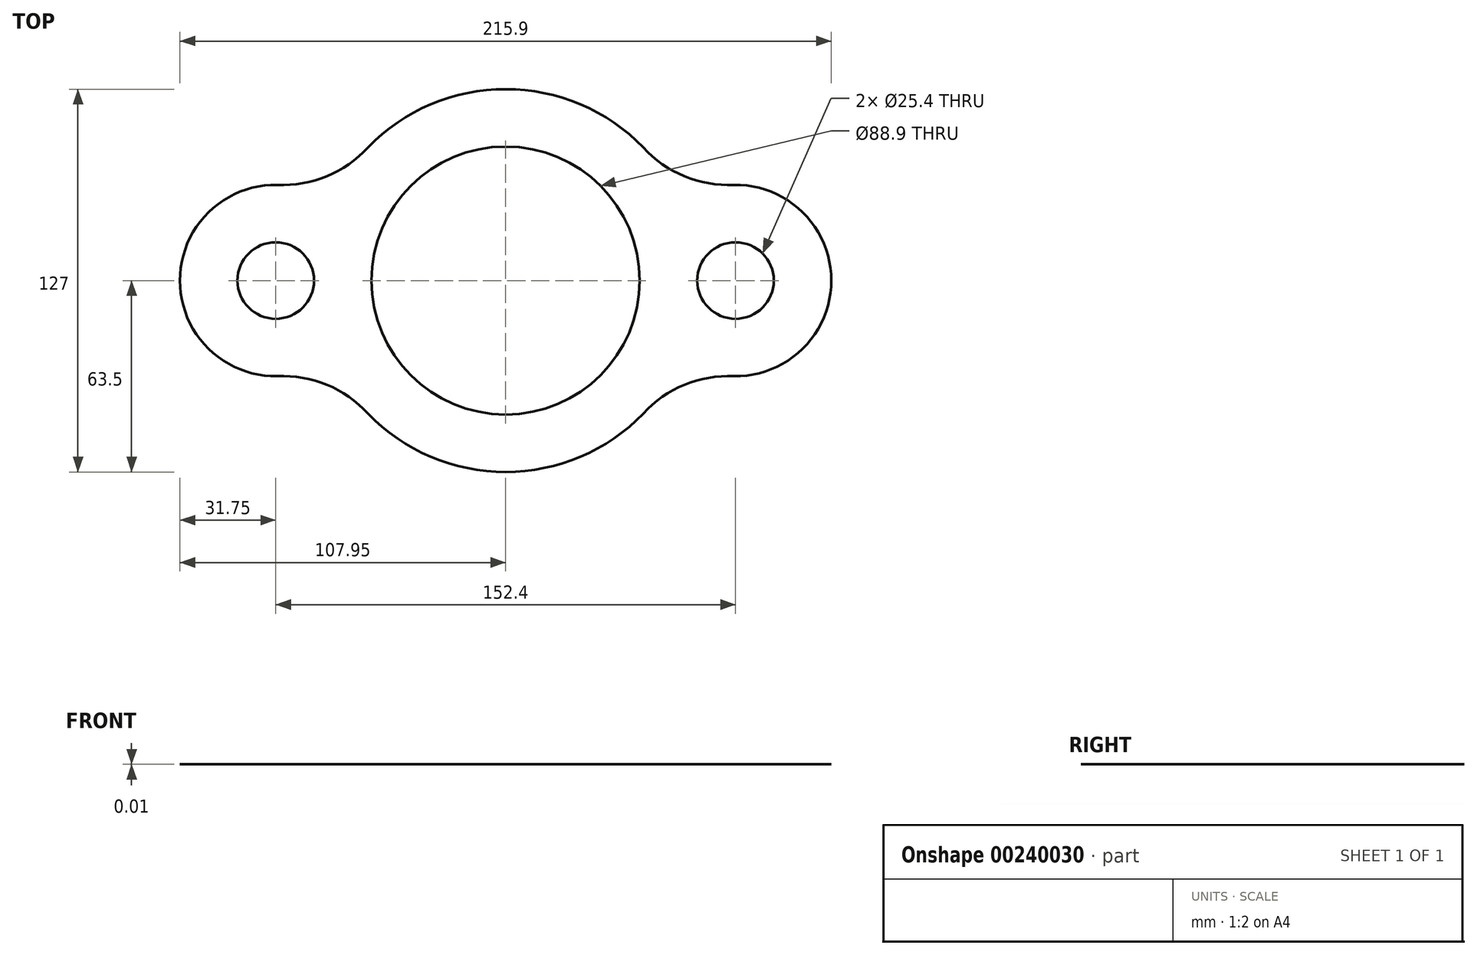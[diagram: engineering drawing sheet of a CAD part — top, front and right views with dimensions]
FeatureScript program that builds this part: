
annotation { "Feature Type Name" : "Feature", "Feature Type Description" : "" }
export const myFeature = defineFeature(function(context is Context, id is Id, definition is map)
    precondition{}
    {
        {
            var Q0;
            Q0=qCreatedBy(makeId("Top.planeOp"),FACE);
            var sketch = newSketch(context, id + "F0", { "sketchPlane" : qUnion([Q0])});
            skCircle(sketch, "E0", {"center": v(0, 0) * mm, "radius": 44.45 * mm});
            skPoint(sketch, "E1", {"position": v(76.2, 0) * mm});
            skCircle(sketch, "E2", {"center": v(76.2, 0) * mm, "radius": 12.7 * mm});
            skPoint(sketch, "E3", {"position": v(-76.2, 0) * mm});
            skCircle(sketch, "E4", {"center": v(-76.2, 0) * mm, "radius": 12.7 * mm});
            skArc(sketch, "E5", {"start": v(-46.64, -43.1) * mm, "mid": v(0, -63.5) * mm, "end": v(46.64, -43.1) * mm});
            skArc(sketch, "E6", {"start": v(74.55, -31.7) * mm, "mid": v(107.95, 0) * mm, "end": v(74.55, 31.7) * mm});
            skArc(sketch, "E7", {"start": v(-74.55, 31.7) * mm, "mid": v(-107.95, 0) * mm, "end": v(-74.55, -31.7) * mm});
            skArc(sketch, "E8", {"start": v(45.63, 44.16) * mm, "mid": v(59.27, 34.59) * mm, "end": v(75.68, 31.75) * mm});
            skArc(sketch, "E9.MirrorC", {"start": v(45.63, -44.16) * mm, "mid": v(59.27, -34.59) * mm, "end": v(75.68, -31.75) * mm});
            skArc(sketch, "E10.MirrorC", {"start": v(-45.63, 44.16) * mm, "mid": v(-59.27, 34.59) * mm, "end": v(-75.68, 31.75) * mm});
            skArc(sketch, "E11.MirrorC", {"start": v(-45.63, -44.16) * mm, "mid": v(-59.27, -34.59) * mm, "end": v(-75.68, -31.75) * mm});
            skArc(sketch, "E12.trimOffspring", {"start": v(63.5, -0.12) * mm, "mid": v(63.5, 0) * mm, "end": v(63.5, 0.12) * mm});
            skLineSegment(sketch, "E13.trimOffspring", {"start": v(44.45, 0) * mm, "end": v(44.45, 0) * mm});
            skArc(sketch, "E14.trimOffspring", {"start": v(46.64, 43.1) * mm, "mid": v(0, 63.5) * mm, "end": v(-46.64, 43.1) * mm});
            skSolve(sketch);
        }
        {
            var Q0;
            Q0=makeQuery(id+"F0.imprint","IMPRINT",FACE,{"disambiguationData":[TD([[makeQuery(id+"F0.imprint","IMPRINT",EDGE,{"derivedFrom":sQuery(id+"F0.wireOp",EDGE,"E4")}),-1.0]])]});
            extrude(context, id + "F1", {"entities" : qUnion([Q0]), "depth" : 1 / 101.6 * mm});
        }
    });
